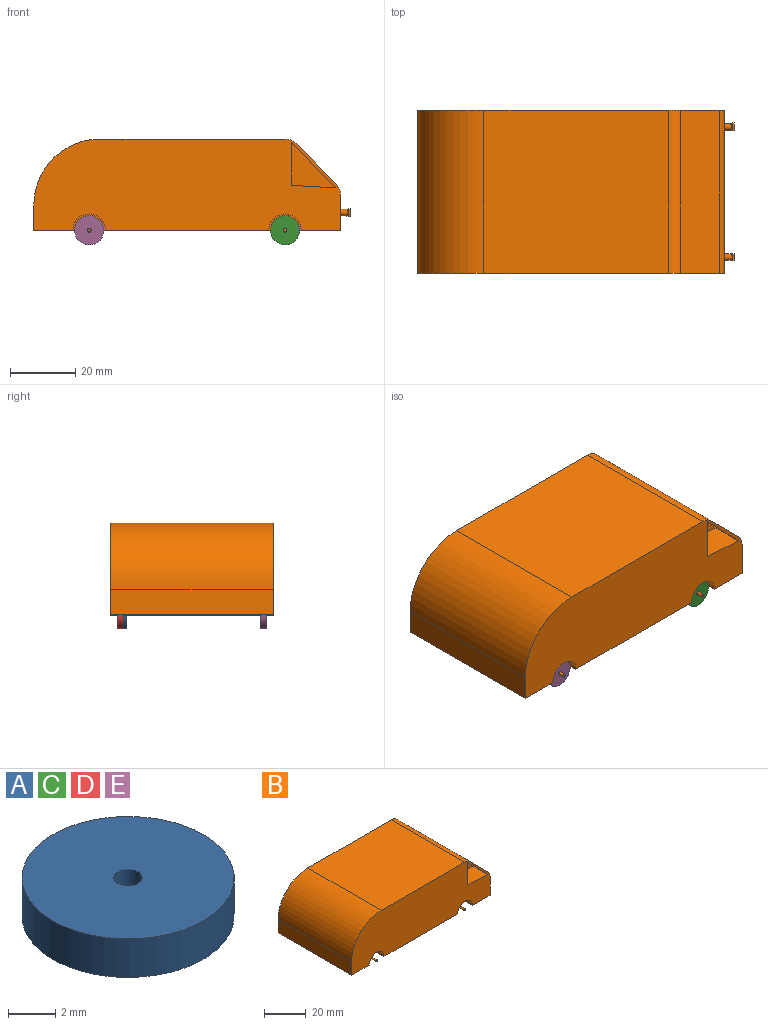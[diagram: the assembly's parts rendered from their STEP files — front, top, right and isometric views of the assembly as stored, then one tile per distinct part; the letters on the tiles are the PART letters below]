
ASSEMBLY  parts=5 mates=4
PART A: 4 faces, bbox 9x9x2 mm
  f0: cylinder r=0.6mm len=2mm, axis (0,0,-1), area 7.5mm2, adj f2,f3
  f1: cylinder r=4.5mm len=9mm, axis (0,0,-1), area 56.5mm2, adj f2,f3
  f2: plane 9x9mm, normal (0,0,1), area 62.5mm2, adj f0,f1
  f3: plane 9x9mm, normal (0,0,-1), area 62.5mm2, adj f0,f1
PART B: 55 faces, bbox 97.1x50x28.5 mm
  f0: plane 94.12x28mm, normal (0,1,0), area 2266.7mm2, adj f6,f7,f10,f11,f12,f13,f14,f15
  f1: plane 14x13.39mm, normal (-0.72,0,-0.69), area 193.7mm2, adj f2,f3,f8,f50
  f2: plane 13.18x10mm, normal (1,0,0), area 131.8mm2, adj f1,f3,f8,f50
  f3: plane 13.39x10mm, normal (0.06,0,1), area 134.1mm2, adj f1,f2,f8,f50
  f4: cylinder r=1mm len=2.4mm, axis (-1,0,0), area 14.5mm2, adj f14,f46,f47,f48,f49
  f5: cylinder r=1mm len=2.3mm, axis (-1,0,0), area 13.5mm2, adj f14,f36,f38,f39,f40
  f6: plane 59.12x50mm, normal (0,0,-1), area 2829.9mm2, adj f0,f8,f9,f10,f11,f17,f18,f19
  f7: plane 50x16.5mm, normal (0,0,-1), area 762mm2, adj f0,f8,f11,f13,f17,f18,f19,f28
  f8: plane 94.12x28mm, normal (0,-1,0), area 2266.7mm2, adj f1,f2,f3,f6,f7,f9,f12,f13
  f9: cylinder r=5mm len=10mm, axis (0,-1,0), area 78.5mm2, adj f6,f8,f12,f20
  f10: cylinder r=5mm len=10mm, axis (0,-1,0), area 141.4mm2, adj f0,f6,f12,f21
  f11: cylinder r=5mm len=10mm, axis (0,-1,0), area 110mm2, adj f0,f6,f7,f18
  f12: plane 50x16.5mm, normal (0,0,-1), area 762mm2, adj f0,f8,f9,f10,f14,f20,f21,f25
  f13: plane 50x7.72mm, normal (-1,0,0), area 386mm2, adj f0,f7,f8,f24
  f14: plane 50x10.93mm, normal (1,0,0), area 540.2mm2, adj f0,f4,f5,f8,f12,f23
  f15: plane 56.77x50mm, normal (0,0,1), area 2838.4mm2, adj f0,f8,f22,f24
  f16: plane 50x12.07mm, normal (0.71,0,0.71), area 853.6mm2, adj f0,f8,f22,f23
  f17: cylinder r=5mm len=10mm, axis (0,-1,0), area 110mm2, adj f6,f7,f8,f19
  f18: plane 10x5mm, normal (0,1,0), area 38.9mm2, adj f6,f7,f11,f28
  f19: plane 10x5mm, normal (0,-1,0), area 38.9mm2, adj f6,f7,f17,f28
  f20: plane 10x5mm, normal (0,-1,0), area 38.9mm2, adj f6,f9,f12,f25
  f21: plane 10x5mm, normal (0,1,0), area 38.9mm2, adj f6,f10,f12,f25
  f22: cylinder r=5mm len=50mm, axis (0,-1,0), area 196.3mm2, adj f0,f8,f15,f16
  f23: cylinder r=5mm len=50mm, axis (0,1,0), area 196.3mm2, adj f0,f8,f14,f16
  f24: cylinder r=20.28mm len=50mm, axis (0,1,0), area 1592.7mm2, adj f0,f8,f13,f15
  f25: cylinder r=0.5mm len=50mm, axis (0,-1,0), area 100.5mm2, adj f6,f12,f20,f21,f26,f27
  f26: plane 1x1mm, normal (0,1,0), area 0.8mm2, adj f25
  f27: plane 1x1mm, normal (0,-1,0), area 0.8mm2, adj f25
  f28: cylinder r=0.5mm len=50mm, axis (0,1,0), area 100.5mm2, adj f6,f7,f18,f19,f29,f30
  f29: plane 1x1mm, normal (0,-1,0), area 0.8mm2, adj f28
  f30: plane 1x1mm, normal (0,1,0), area 0.8mm2, adj f28
  f31: plane 1.2x1mm, normal (0,0.01,-1), area 1.1mm2, adj f32,f35,f36,f37,f38
  f32: plane 1.2x1mm, normal (0,0,-1), area 1.1mm2, adj f31,f33,f36,f37,f40
  f33: plane 2.4x0.5mm, normal (0,1,0), area 1.2mm2, adj f32,f34,f37,f40
  f34: plane 2.4x0.5mm, normal (0,0,1), area 1.2mm2, adj f33,f35,f37,f39
  f35: plane 2.42x0.5mm, normal (0,-1,0), area 1.2mm2, adj f31,f34,f37,f38
  f36: plane 1.4x0.5mm, normal (-1,0,0), area 0.4mm2, adj f5,f31,f32,f38,f40
  f37: plane 2.42x2.4mm, normal (1,0,0), area 5.8mm2, adj f31,f32,f33,f34,f35
  f38: plane 2.42x0.5mm, normal (-0.71,-0.71,0), area 1.1mm2, adj f5,f31,f35,f36,f39
  f39: plane 2.4x0.49mm, normal (-0.71,0,0.71), area 0.9mm2, adj f5,f34,f38,f40
  f40: plane 2.4x0.5mm, normal (-0.71,0.71,0), area 1.1mm2, adj f5,f32,f33,f36,f39
  f41: plane 2.2x0.5mm, normal (0,0,1), area 1.1mm2, adj f42,f44,f45,f49
  f42: plane 2.2x0.5mm, normal (0,-1,0), area 1.1mm2, adj f41,f43,f45,f47
  f43: plane 2.2x0.5mm, normal (0,0,-1), area 1.1mm2, adj f42,f44,f45,f46
  f44: plane 2.2x0.5mm, normal (0,1,0), area 1.1mm2, adj f41,f43,f45,f48
  f45: plane 2.2x2.2mm, normal (1,0,0), area 4.8mm2, adj f41,f42,f43,f44
  f46: plane 2.2x0.39mm, normal (-0.71,0,-0.71), area 0.6mm2, adj f4,f43,f47,f48
  f47: plane 2.2x0.39mm, normal (-0.71,-0.71,0), area 0.6mm2, adj f4,f42,f46,f49
  f48: plane 2.2x0.39mm, normal (-0.71,0.71,0), area 0.6mm2, adj f4,f44,f46,f49
  f49: plane 2.2x0.39mm, normal (-0.71,0,0.71), area 0.6mm2, adj f4,f41,f47,f48
  f50: plane 14x13.39mm, normal (0,-1,0), area 88.2mm2, adj f1,f2,f3
  f51: plane 13.18x5mm, normal (1,0,0), area 65.9mm2, adj f0,f52,f53,f54
  f52: plane 14x13.39mm, normal (-0.72,0,-0.69), area 96.8mm2, adj f0,f51,f53,f54
  f53: plane 13.39x5mm, normal (0.06,0,1), area 67.1mm2, adj f0,f51,f52,f54
  f54: plane 14x13.39mm, normal (0,1,0), area 88.2mm2, adj f51,f52,f53
PART C: same geometry as A
PART D: same geometry as A
PART E: same geometry as A
PLACE A rot(axis=(1,0,0),90deg) t=(29.66,56.44,9.56)mm
PLACE B t=(13.93,24.86,9.56)mm
PLACE C rot(axis=(1,0,0),90deg) t=(29.66,13.44,9.56)mm
PLACE D rot(axis=(1,0,0),90deg) t=(-30.46,57.44,9.56)mm
PLACE E rot(axis=(1,0,0),90deg) t=(-30.46,13.44,9.56)mm
MATE fastened D.f0 <-> B.f28  axis (0,1,0) through (-30.46,57.44,9.56)mm
MATE fastened A.f1 <-> B.f9  axis (0,1,0) through (29.66,56.44,9.56)mm
MATE fastened E.f1 <-> B.f28  axis (0,-1,0) through (-30.46,11.44,9.56)mm
MATE fastened C.f0 <-> B.f9  axis (0,-1,0) through (29.66,11.44,9.56)mm
